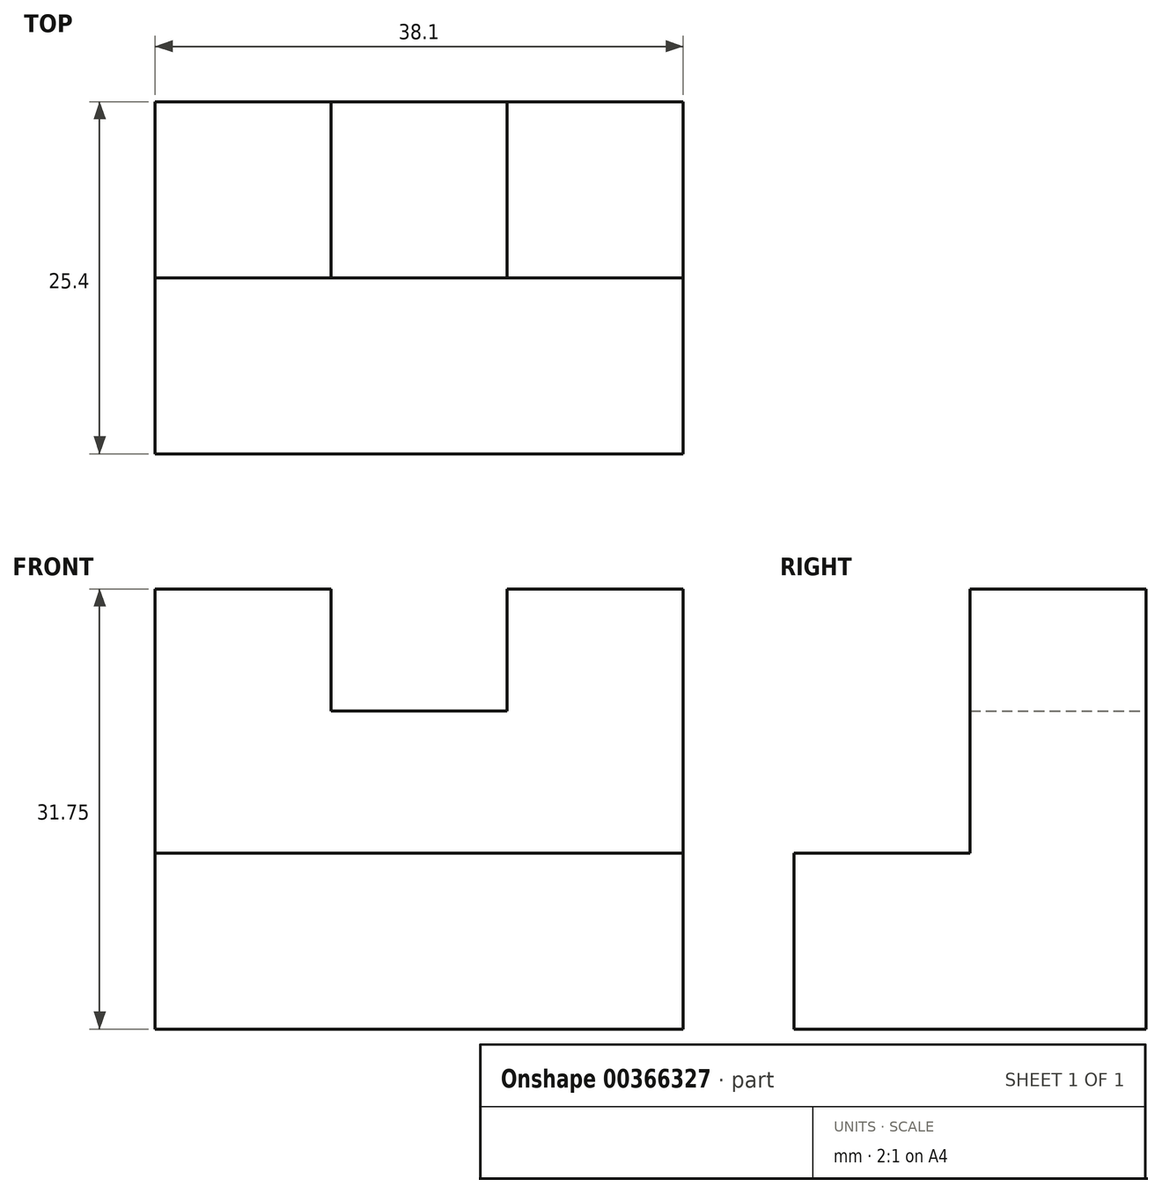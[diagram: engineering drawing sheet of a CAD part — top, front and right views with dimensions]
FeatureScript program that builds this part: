
annotation { "Feature Type Name" : "Feature", "Feature Type Description" : "" }
export const myFeature = defineFeature(function(context is Context, id is Id, definition is map)
    precondition{}
    {
        {
            var Q0;
            Q0=qCreatedBy(makeId("Front.planeOp"),FACE);
            var sketch = newSketch(context, id + "F0", { "sketchPlane" : qUnion([Q0])});
            skLineSegment(sketch, "E0", {"start": v(-48.6, 67.38) * mm, "end": v(-35.9, 67.38) * mm});
            skLineSegment(sketch, "E1", {"start": v(-48.6, 67.38) * mm, "end": v(-48.6, 35.63) * mm});
            skLineSegment(sketch, "E2", {"start": v(-48.6, 35.63) * mm, "end": v(-10.5, 35.63) * mm});
            skLineSegment(sketch, "E3", {"start": v(-10.5, 35.63) * mm, "end": v(-10.5, 67.38) * mm});
            skLineSegment(sketch, "E4", {"start": v(-10.5, 67.38) * mm, "end": v(-23.2, 67.38) * mm});
            skLineSegment(sketch, "E5", {"start": v(-23.2, 67.38) * mm, "end": v(-23.2, 58.59) * mm});
            skLineSegment(sketch, "E6", {"start": v(-23.2, 58.59) * mm, "end": v(-35.9, 58.59) * mm});
            skLineSegment(sketch, "E7", {"start": v(-35.9, 58.59) * mm, "end": v(-35.9, 67.38) * mm});
            skSolve(sketch);
        }
        {
            var Q0;
            Q0 = qSketchRegion(id + "F0", true);
            extrude(context, id + "F1", {"entities" : qUnion([Q0]), "depth" : 12.7 * mm});
        }
        {
            var Q0;
            Q0=makeQuery(id+"F1.opExtrude","CAP_FACE",FACE,{"disambiguationData":[OSD([sQuery(id+"F0.wireOp",EDGE,"E0"),sQuery(id+"F0.wireOp",EDGE,"E1"),sQuery(id+"F0.wireOp",EDGE,"E2"),sQuery(id+"F0.wireOp",EDGE,"E3"),sQuery(id+"F0.wireOp",EDGE,"E4"),sQuery(id+"F0.wireOp",EDGE,"E5"),sQuery(id+"F0.wireOp",EDGE,"E6"),sQuery(id+"F0.wireOp",EDGE,"E7")])],"isStart":false});
            var sketch = newSketch(context, id + "F2", { "sketchPlane" : qUnion([Q0])});
            skLineSegment(sketch, "E8", {"start": v(-48.6, 48.33) * mm, "end": v(-10.5, 48.33) * mm});
            skLineSegment(sketch, "E9", {"start": v(-10.5, 48.33) * mm, "end": v(-10.5, 35.63) * mm});
            skLineSegment(sketch, "E10", {"start": v(-10.5, 35.63) * mm, "end": v(-48.6, 35.63) * mm});
            skLineSegment(sketch, "E11", {"start": v(-48.6, 35.63) * mm, "end": v(-48.6, 48.33) * mm});
            skSolve(sketch);
        }
        {
            var Q0;
            Q0 = qSketchRegion(id + "F2", true);
            extrude(context, id + "F3", {"entities" : qUnion([Q0]), "operationType" : NewBodyOperationType.ADD, "depth" : 12.7 * mm});
        }
    });
